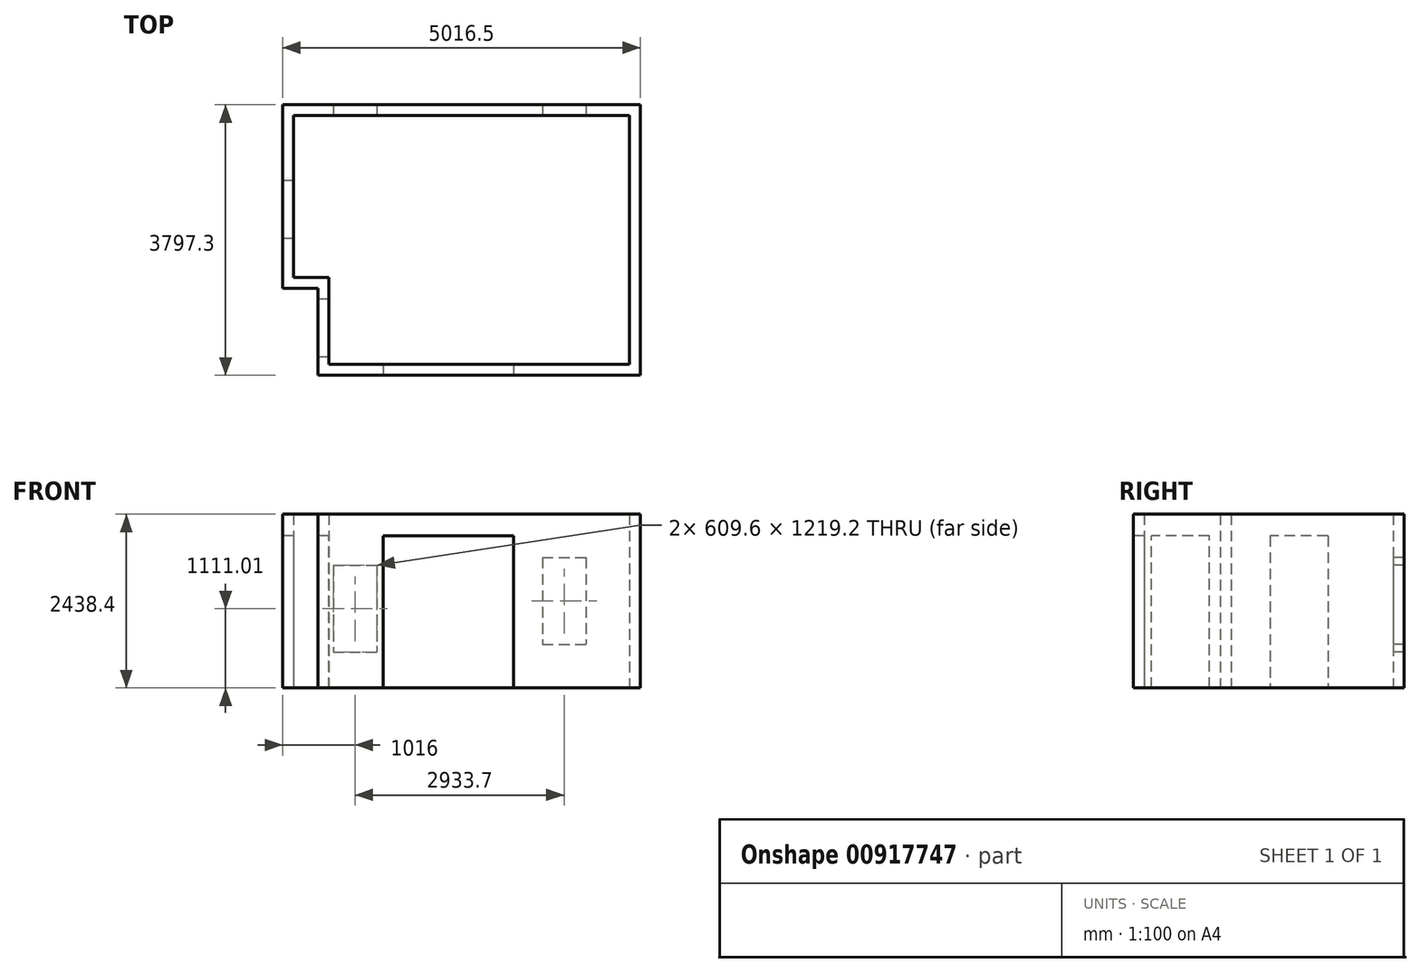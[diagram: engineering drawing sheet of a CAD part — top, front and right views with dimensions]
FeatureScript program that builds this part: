
annotation { "Feature Type Name" : "Feature", "Feature Type Description" : "" }
export const myFeature = defineFeature(function(context is Context, id is Id, definition is map)
    precondition{}
    {
        {
            var Q0;
            Q0=qCreatedBy(makeId("Top.planeOp"),FACE);
            var sketch = newSketch(context, id + "F0", { "sketchPlane" : qUnion([Q0])});
            skLineSegment(sketch, "E0.bottom", {"start": v(2362.23, 1834.13) * mm, "end": v(-2349.47, 1834.13) * mm});
            skLineSegment(sketch, "E0.top", {"start": v(2362.23, -1658.37) * mm, "end": v(-1854.17, -1658.37) * mm});
            skLineSegment(sketch, "E0.left", {"start": v(2362.23, 1834.13) * mm, "end": v(2362.23, -1658.37) * mm});
            skLineSegment(sketch, "E0.right", {"start": v(-2349.47, 1834.13) * mm, "end": v(-2349.47, -439.17) * mm});
            skLineSegment(sketch, "E1", {"start": v(-1854.17, -1658.37) * mm, "end": v(-1854.17, -439.17) * mm});
            skLineSegment(sketch, "E2", {"start": v(-1854.17, -439.17) * mm, "end": v(-2349.47, -439.17) * mm});
            skPoint(sketch, "E3.orphan", {"position": v(-2349.47, -439.17) * mm});
            skSolve(sketch);
        }
        {
            var Q0;
            Q0 = qSketchRegion(id + "F0", true);
            var sketch = newSketch(context, id + "F1", { "sketchPlane" : qUnion([Q0])});
            skLineSegment(sketch, "E4.0", {"start": v(2514.63, 1986.53) * mm, "end": v(2514.63, -1810.77) * mm});
            skLineSegment(sketch, "E4.1", {"start": v(-2501.87, 1986.53) * mm, "end": v(-2501.87, -591.57) * mm});
            skLineSegment(sketch, "E4.2", {"start": v(-2006.57, -591.57) * mm, "end": v(-2501.87, -591.57) * mm});
            skLineSegment(sketch, "E4.3", {"start": v(2514.63, 1986.53) * mm, "end": v(-2501.87, 1986.53) * mm});
            skLineSegment(sketch, "E4.4", {"start": v(-2006.57, -1810.77) * mm, "end": v(-2006.57, -591.57) * mm});
            skLineSegment(sketch, "E4.5", {"start": v(2514.63, -1810.77) * mm, "end": v(-2006.57, -1810.77) * mm});
            skSolve(sketch);
        }
        {
            var Q0;
            Q0 = qSketchRegion(id + "F0", true);
            var Q1;
            Q1 = qSketchRegion(id + "F1", true);
            extrude(context, id + "F2", {"entities" : qUnion([Q0, Q1]), "depth" : 2438.4 * mm, "offsetDistance" : 25.4 * mm});
        }
        {
            var Q0;
            Q0=makeQuery(id+"F2.opExtrude","SWEPT_BODY",BODY,{"disambiguationData":[OSD([sQuery(id+"F0.wireOp",EDGE,"E0.bottom"),sQuery(id+"F0.wireOp",EDGE,"E0.top"),sQuery(id+"F0.wireOp",EDGE,"E0.left"),sQuery(id+"F0.wireOp",EDGE,"E0.right"),sQuery(id+"F0.wireOp",EDGE,"E1"),sQuery(id+"F0.wireOp",EDGE,"E2")])]});
            deleteBodies(context, id + "F3", {"entities" : qUnion([Q0])});
        }
        {
            var Q0;
            Q0 = qSketchRegion(id + "F0", true);
            var sketch = newSketch(context, id + "F4", { "sketchPlane" : qUnion([Q0])});
            skSolve(sketch);
        }
        {
            var Q0;
            Q0=makeQuery(id+"F4.imprint","IMPRINT",FACE,{"disambiguationData":[TD([[makeQuery(id+"F4.imprint","IMPRINT",EDGE,{"derivedFrom":makeQuery(id+"F0.imprint","IMPRINT",EDGE,{"derivedFrom":sQuery(id+"F0.wireOp",EDGE,"E0.bottom")})}),1.0]])]});
            extrude(context, id + "F5", {"entities" : qUnion([Q0]), "operationType" : NewBodyOperationType.REMOVE, "depth" : 2438.4 * mm, "offsetDistance" : 25.4 * mm});
        }
        {
            var Q0;
            Q0=makeQuery(id+"F5.boolean.opBoolean","COPY",FACE,{"derivedFrom":makeQuery(id+"F5.opExtrude","SWEPT_FACE",FACE,{"disambiguationData":[OSD([sQuery(id+"F0.wireOp",EDGE,"E0.bottom")])]})});
            var sketch = newSketch(context, id + "F6", { "sketchPlane" : qUnion([Q0])});
            skLineSegment(sketch, "E5.bottom", {"start": v(-1790.67, 1720.61) * mm, "end": v(-1181.07, 1720.61) * mm});
            skLineSegment(sketch, "E5.top", {"start": v(-1790.67, 501.41) * mm, "end": v(-1181.07, 501.41) * mm});
            skLineSegment(sketch, "E5.left", {"start": v(-1790.67, 1720.61) * mm, "end": v(-1790.67, 501.41) * mm});
            skLineSegment(sketch, "E5.right", {"start": v(-1181.07, 1720.61) * mm, "end": v(-1181.07, 501.41) * mm});
            skLineSegment(sketch, "E6.bottom", {"start": v(1143.03, 1828.8) * mm, "end": v(1752.63, 1828.8) * mm});
            skLineSegment(sketch, "E6.top", {"start": v(1143.03, 609.6) * mm, "end": v(1752.63, 609.6) * mm});
            skLineSegment(sketch, "E6.left", {"start": v(1143.03, 1828.8) * mm, "end": v(1143.03, 609.6) * mm});
            skLineSegment(sketch, "E6.right", {"start": v(1752.63, 1828.8) * mm, "end": v(1752.63, 609.6) * mm});
            skSolve(sketch);
        }
        {
            var Q0;
            Q0=makeQuery(id+"F6.imprint","IMPRINT",FACE,{"disambiguationData":[TD([[makeQuery(id+"F6.imprint","IMPRINT",EDGE,{"derivedFrom":sQuery(id+"F6.wireOp",EDGE,"E6.bottom")}),-1.0]])]});
            var Q1;
            Q1=makeQuery(id+"F6.imprint","IMPRINT",FACE,{"disambiguationData":[TD([[makeQuery(id+"F6.imprint","IMPRINT",EDGE,{"derivedFrom":sQuery(id+"F6.wireOp",EDGE,"E5.bottom")}),-1.0]])]});
            extrude(context, id + "F7", {"entities" : qUnion([Q0, Q1]), "operationType" : NewBodyOperationType.REMOVE, "oppositeDirection" : true, "depth" : 1252.95 * mm, "offsetDistance" : 25.4 * mm});
        }
        {
            var Q0;
            Q0=makeQuery(id+"F2.opExtrude","SWEPT_FACE",FACE,{"disambiguationData":[OSD([sQuery(id+"F1.wireOp",EDGE,"E4.5")])]});
            var sketch = newSketch(context, id + "F8", { "sketchPlane" : qUnion([Q0])});
            skLineSegment(sketch, "E7.bottom", {"start": v(-1092.17, 2133.6) * mm, "end": v(736.63, 2133.6) * mm});
            skLineSegment(sketch, "E7.top", {"start": v(-1092.17, 0) * mm, "end": v(736.63, 0) * mm});
            skLineSegment(sketch, "E7.left", {"start": v(-1092.17, 2133.6) * mm, "end": v(-1092.17, 0) * mm});
            skLineSegment(sketch, "E7.right", {"start": v(736.63, 2133.6) * mm, "end": v(736.63, 0) * mm});
            skSolve(sketch);
        }
        {
            var Q0;
            Q0=makeQuery(id+"F8.imprint","IMPRINT",FACE,{"disambiguationData":[TD([[makeQuery(id+"F8.imprint","IMPRINT",EDGE,{"derivedFrom":sQuery(id+"F8.wireOp",EDGE,"E7.bottom")}),-1.0]])]});
            extrude(context, id + "F9", {"entities" : qUnion([Q0]), "operationType" : NewBodyOperationType.REMOVE, "oppositeDirection" : true, "depth" : 152.4 * mm, "offsetDistance" : 25.4 * mm});
        }
        {
            var Q0;
            Q0=makeQuery(id+"F2.opExtrude","SWEPT_FACE",FACE,{"disambiguationData":[OSD([sQuery(id+"F1.wireOp",EDGE,"E4.4")])]});
            var sketch = newSketch(context, id + "F10", { "sketchPlane" : qUnion([Q0])});
            skLineSegment(sketch, "E8.bottom", {"start": v(743.97, 0) * mm, "end": v(1556.77, 0) * mm});
            skLineSegment(sketch, "E8.top", {"start": v(743.97, 2133.6) * mm, "end": v(1556.77, 2133.6) * mm});
            skLineSegment(sketch, "E8.left", {"start": v(743.97, 0) * mm, "end": v(743.97, 2133.6) * mm});
            skLineSegment(sketch, "E8.right", {"start": v(1556.77, 0) * mm, "end": v(1556.77, 2133.6) * mm});
            skSolve(sketch);
        }
        {
            var Q0;
            Q0=makeQuery(id+"F10.imprint","IMPRINT",FACE,{"disambiguationData":[TD([[makeQuery(id+"F10.imprint","IMPRINT",EDGE,{"derivedFrom":sQuery(id+"F10.wireOp",EDGE,"E8.bottom")}),-1.0]])]});
            extrude(context, id + "F11", {"entities" : qUnion([Q0]), "operationType" : NewBodyOperationType.REMOVE, "oppositeDirection" : true, "depth" : 152.4 * mm, "offsetDistance" : 25.4 * mm});
        }
        {
            var Q0;
            Q0=makeQuery(id+"F2.opExtrude","SWEPT_FACE",FACE,{"disambiguationData":[OSD([sQuery(id+"F1.wireOp",EDGE,"E4.1")])]});
            var sketch = newSketch(context, id + "F12", { "sketchPlane" : qUnion([Q0])});
            skLineSegment(sketch, "E9.bottom", {"start": v(-919.73, 2133.6) * mm, "end": v(-106.93, 2133.6) * mm});
            skLineSegment(sketch, "E9.top", {"start": v(-919.73, 0) * mm, "end": v(-106.93, 0) * mm});
            skLineSegment(sketch, "E9.left", {"start": v(-919.73, 2133.6) * mm, "end": v(-919.73, 0) * mm});
            skLineSegment(sketch, "E9.right", {"start": v(-106.93, 2133.6) * mm, "end": v(-106.93, 0) * mm});
            skSolve(sketch);
        }
        {
            var Q0;
            Q0=makeQuery(id+"F12.imprint","IMPRINT",FACE,{"disambiguationData":[TD([[makeQuery(id+"F12.imprint","IMPRINT",EDGE,{"derivedFrom":sQuery(id+"F12.wireOp",EDGE,"E9.bottom")}),-1.0]])]});
            extrude(context, id + "F13", {"entities" : qUnion([Q0]), "operationType" : NewBodyOperationType.REMOVE, "oppositeDirection" : true, "depth" : 152.4 * mm, "offsetDistance" : 25.4 * mm});
        }
    });
